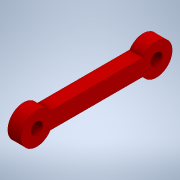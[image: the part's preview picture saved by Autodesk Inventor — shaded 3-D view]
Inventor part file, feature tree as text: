
AUTODESK INVENTOR PART (.ipt)
format: ipt  version: 2020 (Build 240168000, 168)  size: 123,392 bytes
history: native  units: in
note: dims shown in document units (in); Inventor stores cm internally (conversion verified against a paired STEP export)
features: extrude x1, sketch x1
ambient origin geometry x8: Origin, YZ Plane, XZ Plane, XY Plane, X Axis, Y Axis, Z Axis, Center Point
bodies: Solid1 (feature_tree)
feature tree (2):
  extrude  "Extrusion1"  Depth=1.4173in
  sketch  "Sketch1"  dims[d0=0.1378in d1=1.4173in d2=0.1181in d3=0.1181in d4=0.1969in d5=0.1575in d6=0.0in]
